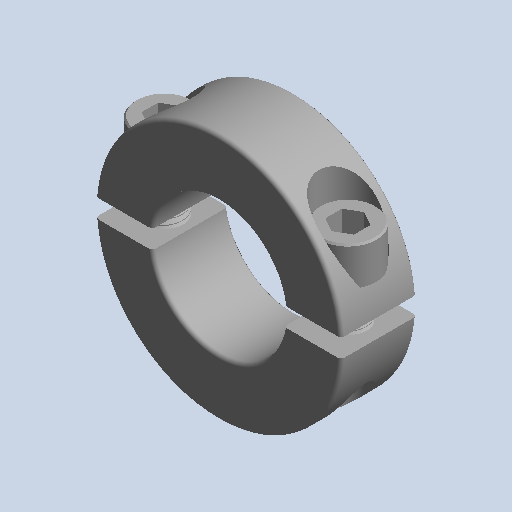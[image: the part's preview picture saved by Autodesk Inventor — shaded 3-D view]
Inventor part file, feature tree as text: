
AUTODESK INVENTOR PART (.ipt)
format: ipt  version: 2022.3 (Build 263350000, 350)  size: 1,279,488 bytes
history: native  units: mm (DEFAULTED — no unit token found)
features: mirror x2, other x2
ambient origin geometry x8: Origin, YZ Plane, XZ Plane, XY Plane, X Axis, Y Axis, Z Axis, Center Point
bodies: Solid1 (feature_tree), Solid2 (feature_tree), Solid3 (feature_tree), Solid4 (feature_tree)
feature tree (4):
  mirror  "Mirror1[1]"
  mirror  "Mirror1[2]"
  other  "Cut-Sweep1"
  other  "LPattern1"
